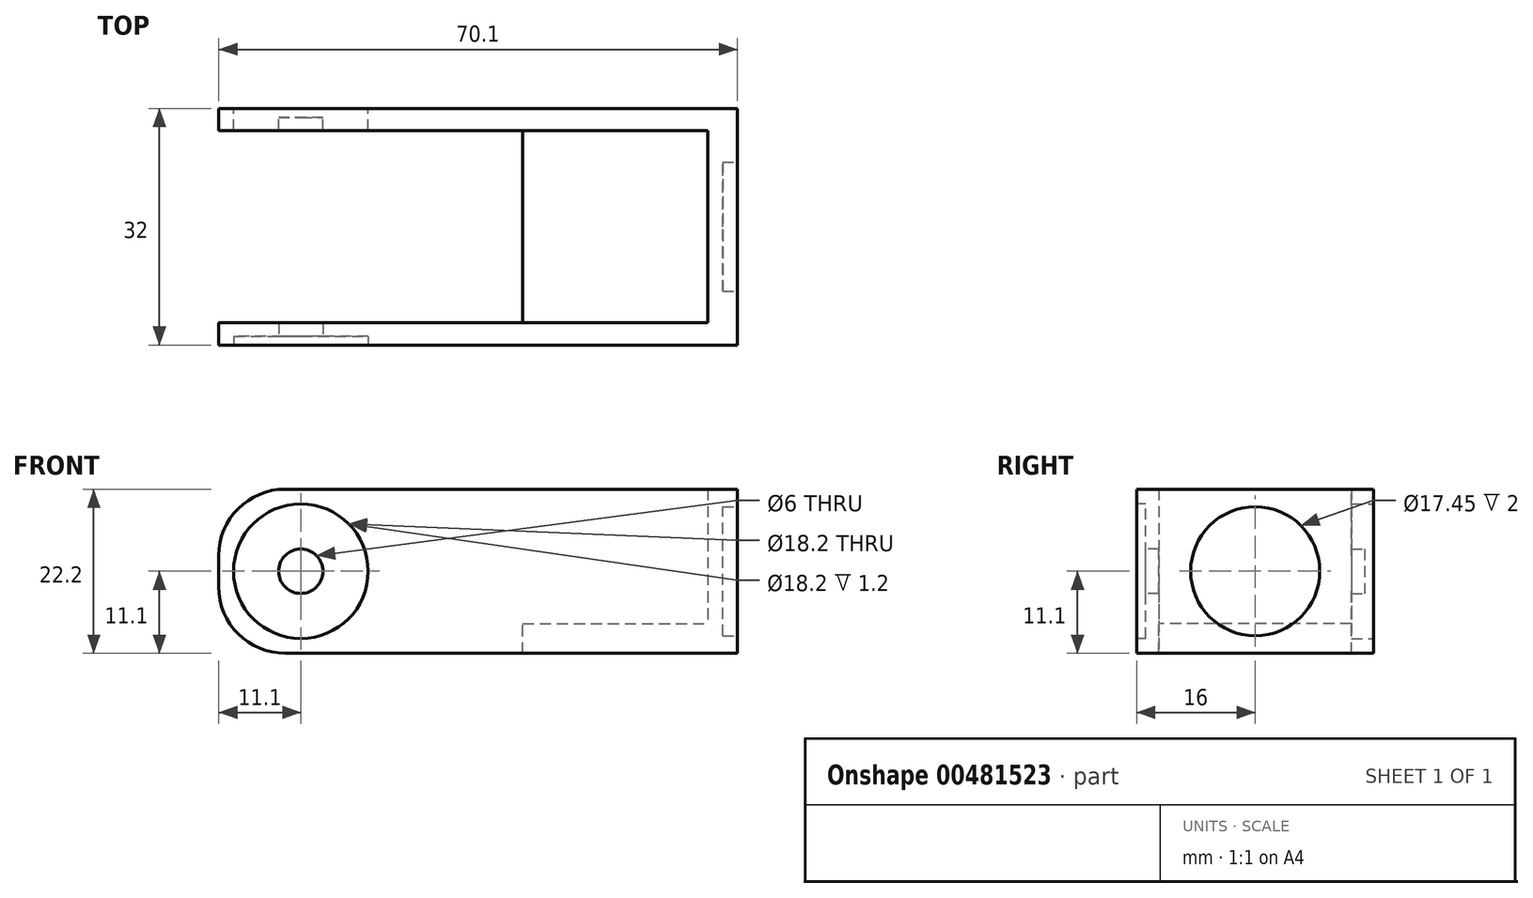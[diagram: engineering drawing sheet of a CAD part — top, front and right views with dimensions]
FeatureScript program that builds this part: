
annotation { "Feature Type Name" : "Feature", "Feature Type Description" : "" }
export const myFeature = defineFeature(function(context is Context, id is Id, definition is map)
    precondition{}
    {
        {
            var Q0;
            Q0=qCreatedBy(makeId("Front.planeOp"),FACE);
            var sketch = newSketch(context, id + "F0", { "sketchPlane" : qUnion([Q0])});
            skCircle(sketch, "E0", {"center": v(0, 0) * mm, "radius": 3 * mm});
            skCircle(sketch, "E1", {"center": v(0, 0) * mm, "radius": 9.1 * mm});
            skLineSegment(sketch, "E2.bottom", {"start": v(-2.1, 11.1) * mm, "end": v(59, 11.1) * mm});
            skLineSegment(sketch, "E2.top", {"start": v(-2.1, -11.1) * mm, "end": v(59, -11.1) * mm});
            skLineSegment(sketch, "E2.left", {"start": v(-11.1, 2.1) * mm, "end": v(-11.1, -2.1) * mm});
            skLineSegment(sketch, "E2.right", {"start": v(59, 11.1) * mm, "end": v(59, -11.1) * mm});
            skLineSegment(sketch, "E3", {"start": v(55, 11.1) * mm, "end": v(55, -11.1) * mm});
            skPoint(sketch, "E4.visualSharp", {"position": v(-11.1, 11.1) * mm});
            skArc(sketch, "E4.filletArc", {"start": v(-2.1, 11.1) * mm, "mid": v(-8.46, 8.46) * mm, "end": v(-11.1, 2.1) * mm});
            skPoint(sketch, "E5.visualSharp", {"position": v(-11.1, -11.1) * mm});
            skArc(sketch, "E5.filletArc", {"start": v(-11.1, -2.1) * mm, "mid": v(-8.46, -8.46) * mm, "end": v(-2.1, -11.1) * mm});
            skLineSegment(sketch, "E6", {"start": v(30, -11.1) * mm, "end": v(30, -7.1) * mm});
            skLineSegment(sketch, "E7", {"start": v(30, -7.1) * mm, "end": v(55, -7.1) * mm});
            skSolve(sketch);
        }
        {
            var Q0;
            Q0=makeQuery(id+"F0.imprint","IMPRINT",FACE,{"disambiguationData":[TD([[makeQuery(id+"F0.imprint","IMPRINT",EDGE,{"derivedFrom":sQuery(id+"F0.wireOp",EDGE,"E1")}),-1.0]])]});
            var Q1;
            Q1=makeQuery(id+"F0.imprint","IMPRINT",FACE,{"disambiguationData":[TD([[makeQuery(id+"F0.imprint","IMPRINT",EDGE,{"derivedFrom":sQuery(id+"F0.wireOp",EDGE,"E0")}),-1.0]])]});
            var Q2;
            Q2=makeQuery(id+"F0.imprint","IMPRINT",FACE,{"disambiguationData":[TD([[makeQuery(id+"F0.imprint","IMPRINT",EDGE,{"derivedFrom":sQuery(id+"F0.wireOp",EDGE,"hC8STci9-6FeU-ZbAn-CVLM-Yexm9Y8LP01g")}),1.0]])]});
            extrude(context, id + "F1", {"entities" : qUnion([Q0, Q1, Q2]), "oppositeDirection" : true, "depth" : 3 * mm, "offsetDistance" : 25 * mm});
        }
        {
            var Q0;
            {var subQ0=sQuery(id+"F0.wireOp",EDGE,"E2.right");Q0=makeQuery(id+"F0.imprint","IMPRINT",FACE,{"disambiguationData":[TD([[makeQuery(id+"F0.imprint","IMPRINT",EDGE,{"derivedFrom":subQ0}),-1.0]])]});}
            var Q1;
            {var subQ3=sQuery(id+"F0.wireOp",EDGE,"E6");Q1=makeQuery(id+"F0.imprint","IMPRINT",FACE,{"disambiguationData":[TD([[makeQuery(id+"F0.imprint","IMPRINT",EDGE,{"derivedFrom":subQ3}),-1.0]])]});}
            extrude(context, id + "F2", {"entities" : qUnion([Q0, Q1]), "operationType" : NewBodyOperationType.ADD, "oppositeDirection" : true, "depth" : 32 * mm, "offsetDistance" : 25 * mm});
        }
        {
            var Q0;
            Q0=makeQuery(id+"F2.opExtrude","CAP_FACE",FACE,{"disambiguationData":[OSD([sQuery(id+"F0.wireOp",EDGE,"E2.bottom"),sQuery(id+"F0.wireOp",EDGE,"E2.top"),sQuery(id+"F0.wireOp",EDGE,"E2.right"),sQuery(id+"F0.wireOp",EDGE,"E3")])],"isStart":false});
            var sketch = newSketch(context, id + "F3", { "sketchPlane" : qUnion([Q0])});
            skLineSegment(sketch, "E8.0.0", {"start": v(-30, -11.1) * mm, "end": v(-30, -7.1) * mm});
            skLineSegment(sketch, "E8.0.1", {"start": v(-30, -7.1) * mm, "end": v(-55, -7.1) * mm});
            skLineSegment(sketch, "E8.0.2", {"start": v(-55, -7.1) * mm, "end": v(-55, 11.1) * mm});
            skLineSegment(sketch, "E8.0.3", {"start": v(-55, 11.1) * mm, "end": v(2.1, 11.1) * mm});
            skArc(sketch, "E8.0.4", {"start": v(2.1, 11.1) * mm, "mid": v(8.46, 8.46) * mm, "end": v(11.1, 2.1) * mm});
            skLineSegment(sketch, "E8.0.5", {"start": v(11.1, 2.1) * mm, "end": v(11.1, -2.1) * mm});
            skArc(sketch, "E8.0.6", {"start": v(11.1, -2.1) * mm, "mid": v(8.46, -8.46) * mm, "end": v(2.1, -11.1) * mm});
            skLineSegment(sketch, "E8.0.7", {"start": v(2.1, -11.1) * mm, "end": v(-30, -11.1) * mm});
            skCircle(sketch, "E8.1", {"center": v(0, 0) * mm, "radius": 3 * mm});
            skCircle(sketch, "E8.2", {"center": v(0, 0) * mm, "radius": 9.1 * mm});
            skSolve(sketch);
        }
        {
            var Q0;
            Q0=makeQuery(id+"F3.imprint","IMPRINT",FACE,{"disambiguationData":[TD([[makeQuery(id+"F3.imprint","IMPRINT",EDGE,{"derivedFrom":sQuery(id+"F3.wireOp",EDGE,"E8.0.0")}),-1.0]])]});
            var Q1;
            Q1=makeQuery(id+"F3.imprint","IMPRINT",FACE,{"disambiguationData":[TD([[makeQuery(id+"F3.imprint","IMPRINT",EDGE,{"derivedFrom":sQuery(id+"F3.wireOp",EDGE,"E8.1")}),1.0]])]});
            extrude(context, id + "F4", {"entities" : qUnion([Q0, Q1]), "operationType" : NewBodyOperationType.ADD, "oppositeDirection" : true, "depth" : 3 * mm, "offsetDistance" : 25 * mm});
        }
        {
            var Q0;
            Q0=makeQuery(id+"F0.imprint","IMPRINT",FACE,{"disambiguationData":[TD([[makeQuery(id+"F0.imprint","IMPRINT",EDGE,{"derivedFrom":sQuery(id+"F0.wireOp",EDGE,"E0")}),-1.0]])]});
            extrude(context, id + "F5", {"entities" : qUnion([Q0]), "operationType" : NewBodyOperationType.REMOVE, "oppositeDirection" : true, "depth" : 1.2 * mm, "offsetDistance" : 25 * mm});
        }
        {
            var Q0;
            Q0=makeQuery(id+"F2.opExtrude","SWEPT_FACE",FACE,{"disambiguationData":[OSD([sQuery(id+"F0.wireOp",EDGE,"E2.right")])]});
            var sketch = newSketch(context, id + "F6", { "sketchPlane" : qUnion([Q0])});
            skCircle(sketch, "E9", {"center": v(16, 0) * mm, "radius": 8.72 * mm});
            skSolve(sketch);
        }
        {
            var Q0;
            Q0=makeQuery(id+"F6.imprint","IMPRINT",FACE,{"disambiguationData":[TD([[makeQuery(id+"F6.imprint","IMPRINT",EDGE,{"derivedFrom":sQuery(id+"F6.wireOp",EDGE,"E9")}),1.0]])]});
            extrude(context, id + "F7", {"entities" : qUnion([Q0]), "operationType" : NewBodyOperationType.REMOVE, "oppositeDirection" : true, "depth" : 2 * mm, "offsetDistance" : 25 * mm});
        }
        {
            var Q0;
            Q0=makeQuery(id+"F3.imprint","IMPRINT",FACE,{"disambiguationData":[TD([[makeQuery(id+"F3.imprint","IMPRINT",EDGE,{"derivedFrom":sQuery(id+"F3.wireOp",EDGE,"E8.1")}),1.0]])]});
            extrude(context, id + "F8", {"entities" : qUnion([Q0]), "operationType" : NewBodyOperationType.REMOVE, "oppositeDirection" : true, "depth" : 1.2 * mm, "offsetDistance" : 25 * mm});
        }
    });
